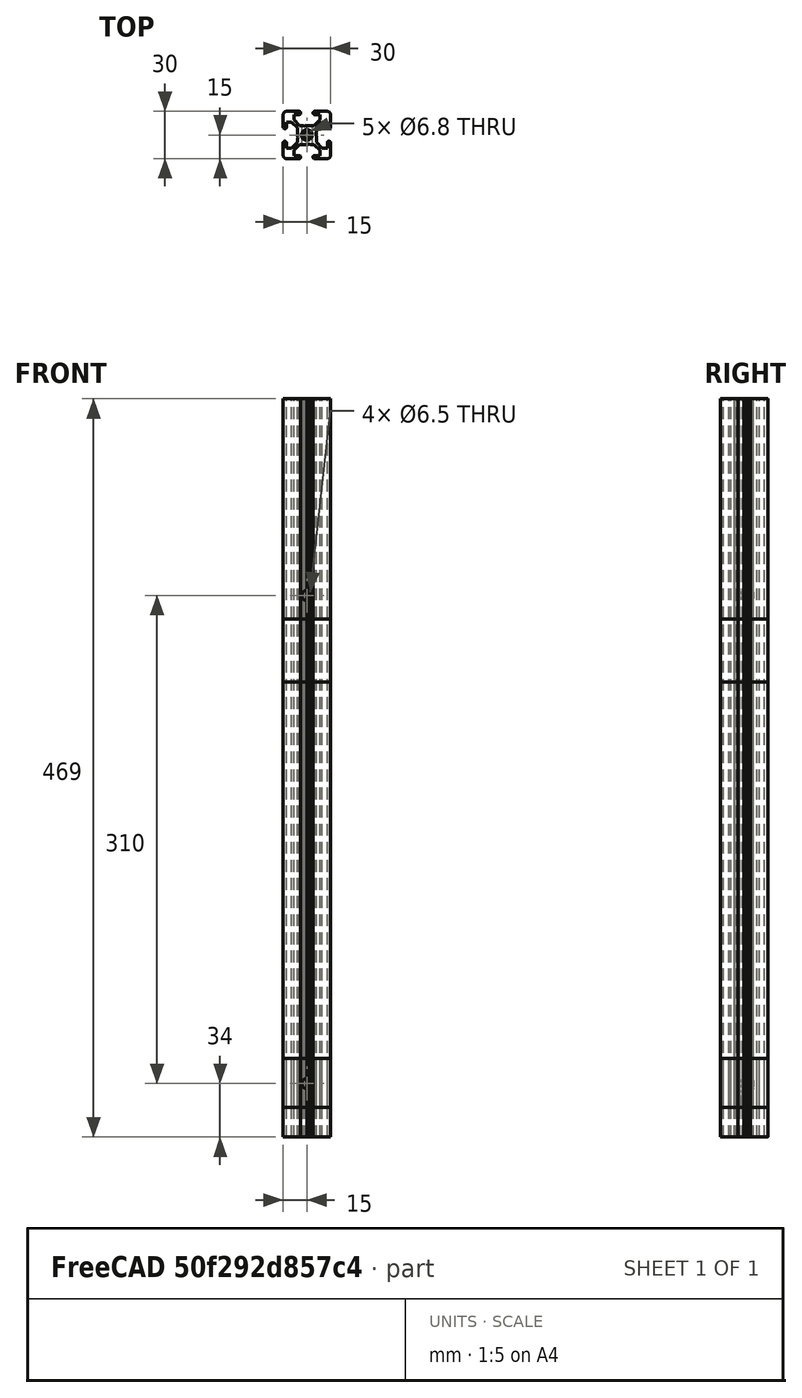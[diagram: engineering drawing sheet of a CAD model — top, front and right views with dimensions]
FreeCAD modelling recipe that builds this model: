
FCSTD DOCUMENT  (FreeCAD 0.18R16146 (Git))
Label: 3030-tslot
License: Other
LicenseURL: GPL3
objects: Part::Feature×10, Part::Extrusion×4, Part::Cylinder×3, Part::MultiFuse×1, Part::Cut×1
note: 19 computed .brp shape members not serialized (recipe doc carries the construction recipe); baked Part::Feature solids carry a one-line shape summary decoded from their .brp

FEATURE [Part::Feature] Part__Feature  label="_GNFS6-3030-50"
  Placement = pos=(0,0,31) rot=(0,0,1;0rad)
  shape: bbox 30 x 30 x 50 mm, 95 faces (baked)
FEATURE [Part::Cylinder] Cylinder
  Angle = 360
  AttacherType = Attacher::AttachEngine3D
  Height = 10
  Radius = 2
FEATURE [Part::Feature] Part__Feature_cs  label="profile-template"
  Placement = pos=(0,0,-1) rot=(0,0,1;0rad)
  shape: bbox 30 x 30 x 3e-07 mm, 0 faces, 0 solids (baked)
FEATURE [Part::Feature] Part__Feature_cs001  label="profile-template001"
  Placement = pos=(0,0,-1) rot=(0,0,1;0rad)
  shape: bbox 30 x 30 x 3e-07 mm, 0 faces, 0 solids (baked)
FEATURE [Part::Extrusion] Extrude  label="310"
  Base = -> Part__Feature_cs001
  Dir = (0,0,1)
  DirMode = 2
  FaceMakerClass = Part::FaceMakerBullseye
  LengthFwd = 310
  LengthRev = 0
  Solid = true
  Symmetric = false
FEATURE [Part::Feature] Extrude001  label="3030-310mm"
  shape: bbox 30 x 30 x 310 mm, 95 faces (baked)
FEATURE [Part::Feature] Part__Feature_cs002  label="profile-template002"
  Placement = pos=(0,0,-1) rot=(0,0,1;0rad)
  shape: bbox 30 x 30 x 3e-07 mm, 0 faces, 0 solids (baked)
FEATURE [Part::Extrusion] Extrude002  label="450"
  Base = -> Part__Feature_cs002
  Dir = (0,0,1)
  DirMode = 2
  FaceMakerClass = Part::FaceMakerBullseye
  LengthFwd = 450
  LengthRev = 0
  Solid = true
  Symmetric = false
FEATURE [Part::Feature] Extrude002001  label="3030-450mm001"
  shape: bbox 30 x 30 x 450 mm, 95 faces (baked)
FEATURE [Part::Feature] Part__Feature_cs003  label="profile-template003"
  Placement = pos=(0,0,-1) rot=(0,0,1;0rad)
  shape: bbox 30 x 30 x 3e-07 mm, 0 faces, 0 solids (baked)
FEATURE [Part::Extrusion] Extrude002002  label="3030-270mm"
  Base = -> Part__Feature_cs003
  Dir = (0,0,1)
  DirMode = 2
  FaceMakerClass = Part::FaceMakerBullseye
  LengthFwd = 270
  LengthRev = 0
  Solid = true
  Symmetric = false
FEATURE [Part::Feature] Extrude002002001  label="3030-270mm001"
  shape: bbox 30 x 30 x 270 mm, 95 faces (baked)
FEATURE [Part::Feature] Part__Feature_cs004  label="profile-template004"
  Placement = pos=(0,0,-1) rot=(0,0,1;0rad)
  shape: bbox 30 x 30 x 3e-07 mm, 0 faces, 0 solids (baked)
FEATURE [Part::Extrusion] Extrude002002002
  Base = -> Part__Feature_cs004
  Dir = (0,0,1)
  DirMode = 2
  FaceMakerClass = Part::FaceMakerBullseye
  LengthFwd = 450
  LengthRev = 0
  Solid = true
  Symmetric = false
FEATURE [Part::Cylinder] Cylinder001
  Angle = 360
  AttacherType = Attacher::AttachEngine3D
  Height = 40
  Placement = pos=(0,16,15) rot=(1,0,0;1.5708rad)
  Radius = 3.25
FEATURE [Part::Cylinder] Cylinder002
  Angle = 360
  AttacherType = Attacher::AttachEngine3D
  Height = 40
  Placement = pos=(0,16,325) rot=(1,0,0;1.5708rad)
  Radius = 3.25
FEATURE [Part::MultiFuse] Fusion
  Shapes = -> [Cylinder002,Cylinder001]
FEATURE [Part::Cut] Cut
  Base = -> Extrude002002002
  Tool = -> Fusion
FEATURE [Part::Feature] Cut001  label="3030-450mm"
  shape: bbox 30 x 30 x 450 mm, 123 faces (baked)
